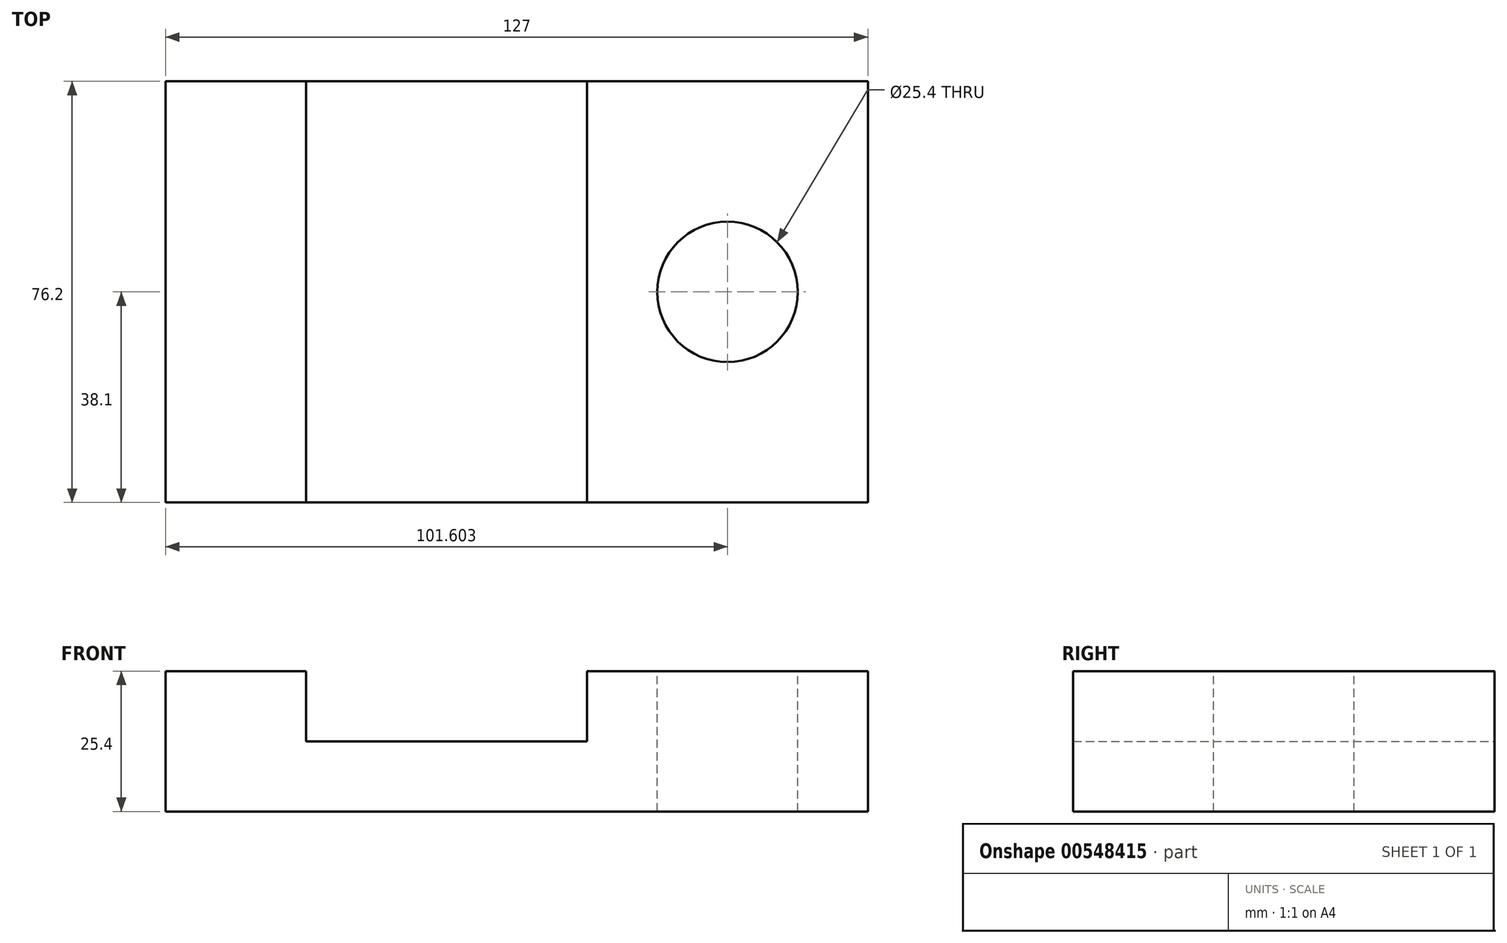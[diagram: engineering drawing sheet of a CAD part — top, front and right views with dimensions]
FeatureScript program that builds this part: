
annotation { "Feature Type Name" : "Feature", "Feature Type Description" : "" }
export const myFeature = defineFeature(function(context is Context, id is Id, definition is map)
    precondition{}
    {
        {
            var Q0;
            Q0=qCreatedBy(makeId("Front.planeOp"),FACE);
            var sketch = newSketch(context, id + "F0", { "sketchPlane" : qUnion([Q0])});
            skLineSegment(sketch, "E0", {"start": v(-73.28, -16.6) * mm, "end": v(-73.28, -42) * mm});
            skLineSegment(sketch, "E1", {"start": v(-73.28, -42) * mm, "end": v(53.72, -42) * mm});
            skLineSegment(sketch, "E2", {"start": v(53.72, -42) * mm, "end": v(53.72, -16.6) * mm});
            skLineSegment(sketch, "E3", {"start": v(53.72, -16.6) * mm, "end": v(2.92, -16.6) * mm});
            skLineSegment(sketch, "E4", {"start": v(2.92, -16.6) * mm, "end": v(2.92, -29.3) * mm});
            skLineSegment(sketch, "E5", {"start": v(2.92, -29.3) * mm, "end": v(-47.88, -29.3) * mm});
            skLineSegment(sketch, "E6", {"start": v(-47.88, -29.3) * mm, "end": v(-47.88, -16.6) * mm});
            skLineSegment(sketch, "E7", {"start": v(-47.88, -16.6) * mm, "end": v(-73.28, -16.6) * mm});
            skSolve(sketch);
        }
        {
            var Q0;
            Q0=makeQuery(id+"F0.imprint","IMPRINT",FACE,{"disambiguationData":[TD([[makeQuery(id+"F0.imprint","IMPRINT",EDGE,{"derivedFrom":sQuery(id+"F0.wireOp",EDGE,"E0")}),1.0]])]});
            extrude(context, id + "F1", {"entities" : qUnion([Q0]), "depth" : 76.2 * mm, "offsetDistance" : 25.4 * mm});
        }
        {
            var Q0;
            Q0=makeQuery(id+"F1.opExtrude","SWEPT_FACE",FACE,{"disambiguationData":[OSD([sQuery(id+"F0.wireOp",EDGE,"E3")])]});
            var sketch = newSketch(context, id + "F2", { "sketchPlane" : qUnion([Q0])});
            skCircle(sketch, "E8", {"center": v(28.32, -38.1) * mm, "radius": 12.7 * mm});
            skSolve(sketch);
        }
        {
            var Q0;
            Q0=sQuery(id+"F2.wireOp",VERTEX,"E8.center");
            var Q1;
            Q1=makeQuery(id+"F1.opExtrude","SWEPT_BODY",BODY,{"disambiguationData":[OSD([sQuery(id+"F0.wireOp",EDGE,"E0"),sQuery(id+"F0.wireOp",EDGE,"E1"),sQuery(id+"F0.wireOp",EDGE,"E2"),sQuery(id+"F0.wireOp",EDGE,"E3"),sQuery(id+"F0.wireOp",EDGE,"E4"),sQuery(id+"F0.wireOp",EDGE,"E5"),sQuery(id+"F0.wireOp",EDGE,"E6"),sQuery(id+"F0.wireOp",EDGE,"E7")])]});
            hole(context, id + "F3", {"style" : HoleStyle.SIMPLE, "endStyle" : HoleEndStyle.THROUGH, "holeDiameter" : 25.4 * mm, "isTappedThrough" : true, "tappedDepth" : 12.7 * mm, "tapClearance" : 3, "locations" : qUnion([Q0]), "scope" : qUnion([Q1])});
        }
    });
